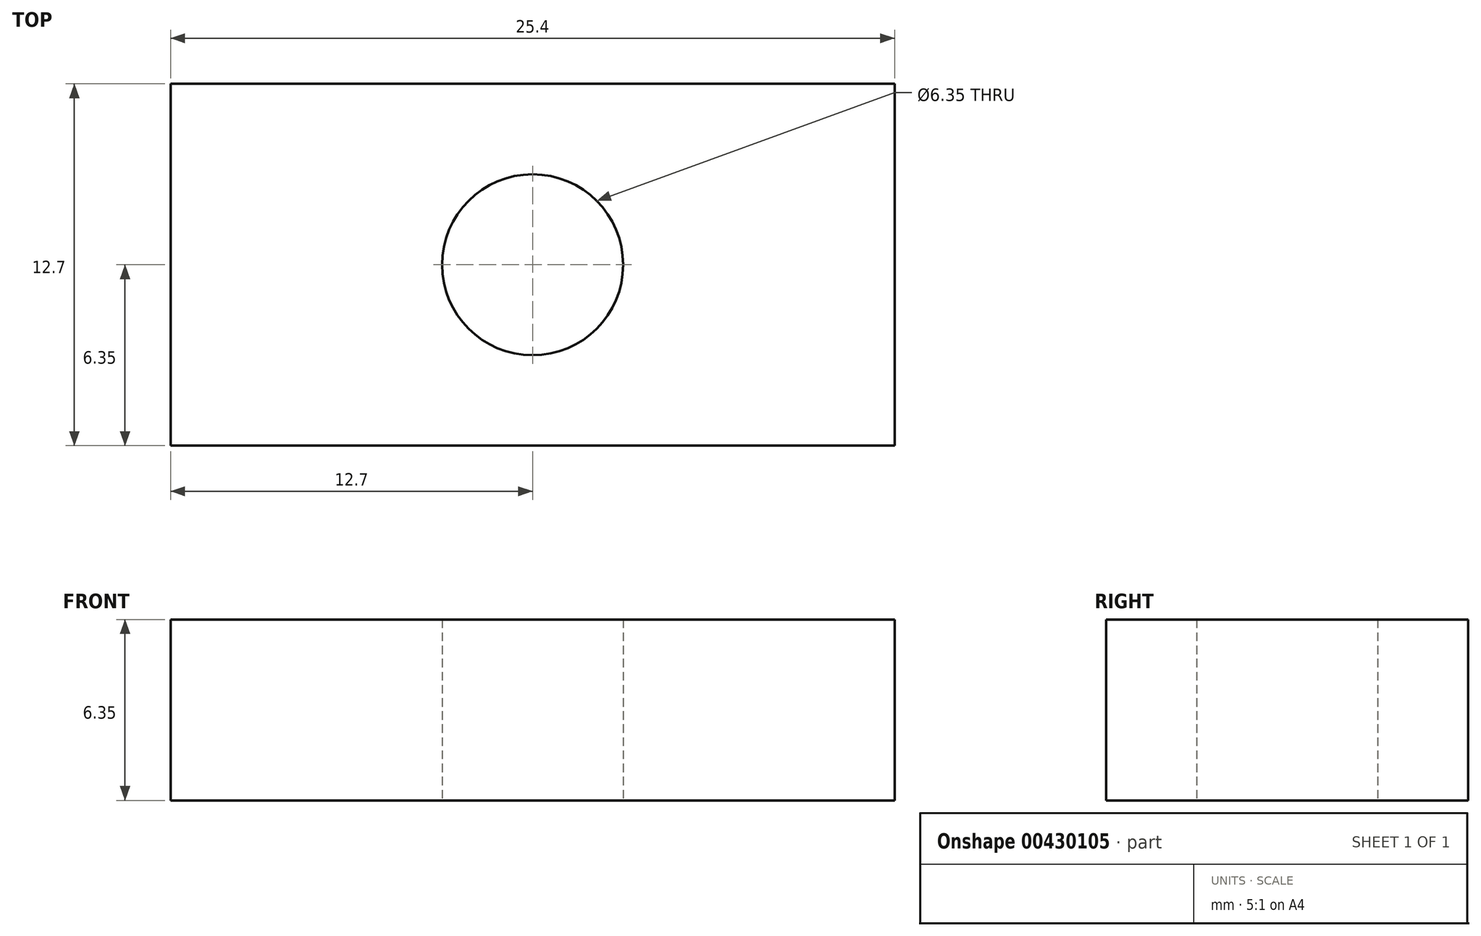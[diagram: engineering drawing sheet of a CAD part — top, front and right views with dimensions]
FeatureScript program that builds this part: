
annotation { "Feature Type Name" : "Feature", "Feature Type Description" : "" }
export const myFeature = defineFeature(function(context is Context, id is Id, definition is map)
    precondition{}
    {
        {
            var Q0;
            Q0=qCreatedBy(makeId("Top.planeOp"),FACE);
            var sketch = newSketch(context, id + "F0", { "sketchPlane" : qUnion([Q0])});
            skLineSegment(sketch, "E0.bottom", {"start": v(0, 0) * mm, "end": v(25.4, 0) * mm});
            skLineSegment(sketch, "E0.top", {"start": v(0, -12.7) * mm, "end": v(25.4, -12.7) * mm});
            skLineSegment(sketch, "E0.left", {"start": v(0, 0) * mm, "end": v(0, -12.7) * mm});
            skLineSegment(sketch, "E0.right", {"start": v(25.4, 0) * mm, "end": v(25.4, -12.7) * mm});
            skLineSegment(sketch, "E1", {"start": v(0, -6.35) * mm, "end": v(25.4, -6.35) * mm, "construction": true});
            skCircle(sketch, "E2", {"center": v(12.7, -6.35) * mm, "radius": 3.18 * mm});
            skSolve(sketch);
        }
        {
            var Q0;
            Q0=makeQuery(id+"F0.imprint","IMPRINT",FACE,{"disambiguationData":[TD([[makeQuery(id+"F0.imprint","IMPRINT",EDGE,{"derivedFrom":sQuery(id+"F0.wireOp",EDGE,"E0.bottom")}),-1.0]])]});
            extrude(context, id + "F1", {"entities" : qUnion([Q0]), "depth" : 6.35 * mm});
        }
    });
